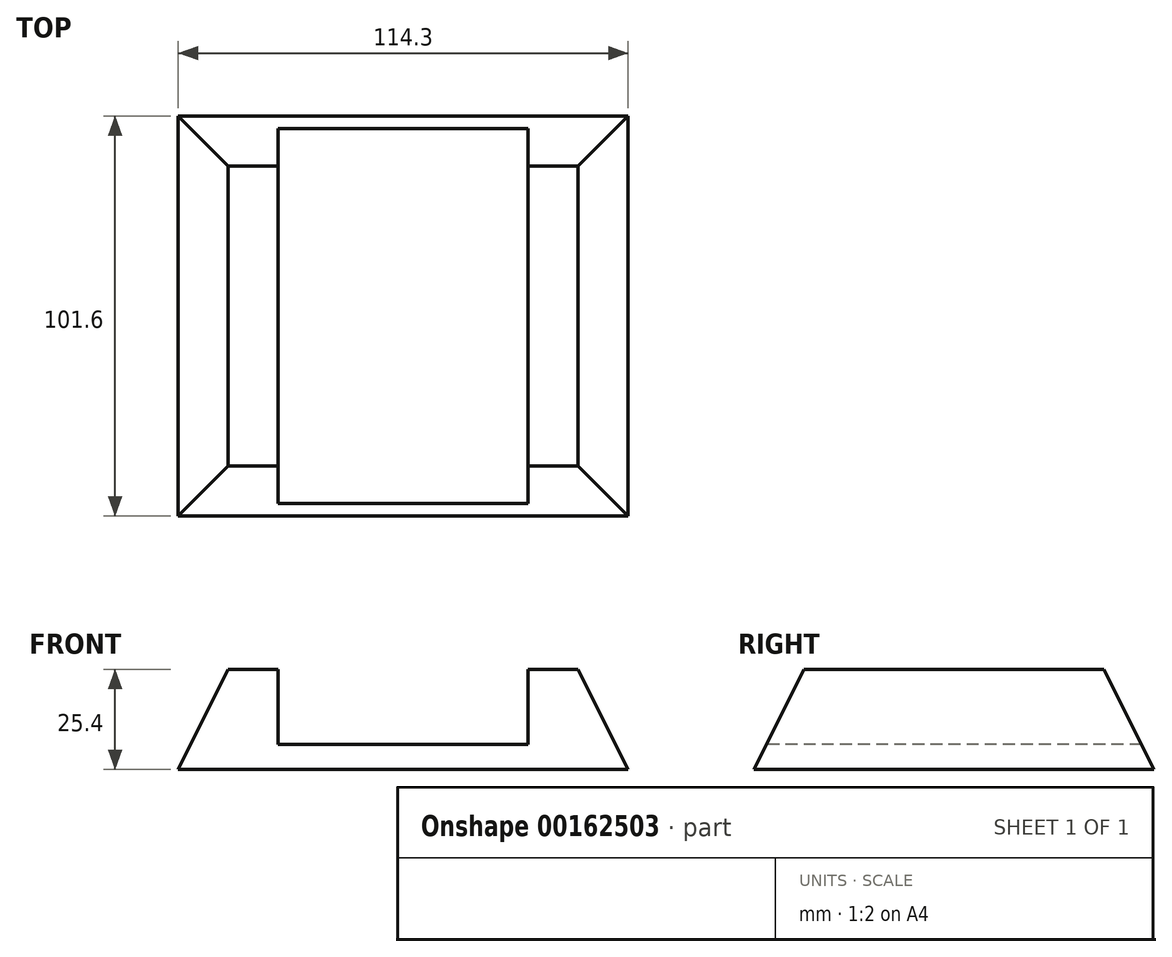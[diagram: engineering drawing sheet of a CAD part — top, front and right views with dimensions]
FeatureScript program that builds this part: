
annotation { "Feature Type Name" : "Feature", "Feature Type Description" : "" }
export const myFeature = defineFeature(function(context is Context, id is Id, definition is map)
    precondition{}
    {
        {
            var Q0;
            Q0=qCreatedBy(makeId("Top.planeOp"),FACE);
            var sketch = newSketch(context, id + "F0", { "sketchPlane" : qUnion([Q0])});
            skLineSegment(sketch, "E0.bottom", {"start": v(-57.15, -50.8) * mm, "end": v(57.15, -50.8) * mm});
            skLineSegment(sketch, "E0.top", {"start": v(-57.15, 50.8) * mm, "end": v(57.15, 50.8) * mm});
            skLineSegment(sketch, "E0.left", {"start": v(-57.15, -50.8) * mm, "end": v(-57.15, 50.8) * mm});
            skLineSegment(sketch, "E0.right", {"start": v(57.15, -50.8) * mm, "end": v(57.15, 50.8) * mm});
            skPoint(sketch, "E0.middle", {"position": v(0, 0) * mm});
            skSolve(sketch);
        }
        {
            var Q0;
            Q0=qCreatedBy(makeId("Top.planeOp"),FACE);
            cPlane(context, id + "F1", {"entities" : qUnion([Q0]), "cplaneType" : CPlaneType.OFFSET, "offset" : 25.4 * mm, "width" : 152.4 * mm, "height" : 152.4 * mm});
        }
        {
            var Q0;
            Q0=qCreatedBy(id+"F1.planeOp",FACE);
            var sketch = newSketch(context, id + "F2", { "sketchPlane" : qUnion([Q0])});
            skLineSegment(sketch, "E1.bottom", {"start": v(-44.45, 38.1) * mm, "end": v(44.45, 38.1) * mm});
            skLineSegment(sketch, "E1.top", {"start": v(-44.45, -38.1) * mm, "end": v(44.45, -38.1) * mm});
            skLineSegment(sketch, "E1.left", {"start": v(-44.45, 38.1) * mm, "end": v(-44.45, -38.1) * mm});
            skLineSegment(sketch, "E1.right", {"start": v(44.45, 38.1) * mm, "end": v(44.45, -38.1) * mm});
            skPoint(sketch, "E1.middle", {"position": v(0, 0) * mm});
            skSolve(sketch);
        }
        {
            var Q0;
            Q0=makeQuery(id+"F2.imprint","IMPRINT",FACE,{"disambiguationData":[TD([[makeQuery(id+"F2.imprint","IMPRINT",EDGE,{"derivedFrom":sQuery(id+"F2.wireOp",EDGE,"E1.bottom")}),-1.0]])]});
            var Q1;
            Q1=makeQuery(id+"F0.imprint","IMPRINT",FACE,{"disambiguationData":[TD([[makeQuery(id+"F0.imprint","IMPRINT",EDGE,{"derivedFrom":sQuery(id+"F0.wireOp",EDGE,"E0.bottom")}),1.0]])]});
            loft(context, id + "F3", {"sheetProfilesArray" : [{ "sheetProfileEntities" : qUnion([Q0]) }, { "sheetProfileEntities" : qUnion([Q1]) }]});
        }
        {
            var Q0;
            Q0=makeQuery(id+"F3.opLoft","CAP_FACE",FACE,{"disambiguationData":[OSD([makeQuery(id+"F2.imprint","IMPRINT",FACE,{"disambiguationData":[TD([[makeQuery(id+"F2.imprint","IMPRINT",EDGE,{"derivedFrom":sQuery(id+"F2.wireOp",EDGE,"E1.bottom")}),-1.0]])]})])],"isStart":true});
            var sketch = newSketch(context, id + "F4", { "sketchPlane" : qUnion([Q0])});
            skLineSegment(sketch, "E2.bottom", {"start": v(-31.75, 96.14) * mm, "end": v(31.75, 96.14) * mm});
            skLineSegment(sketch, "E2.top", {"start": v(-31.75, -96.14) * mm, "end": v(31.75, -96.14) * mm});
            skLineSegment(sketch, "E2.left", {"start": v(-31.75, 96.14) * mm, "end": v(-31.75, -96.14) * mm});
            skLineSegment(sketch, "E2.right", {"start": v(31.75, 96.14) * mm, "end": v(31.75, -96.14) * mm});
            skPoint(sketch, "E2.middle", {"position": v(0, 0) * mm});
            skSolve(sketch);
        }
        {
            var Q0;
            Q0 = qSketchRegion(id + "F4", true);
            extrude(context, id + "F5", {"entities" : qUnion([Q0]), "operationType" : NewBodyOperationType.REMOVE, "oppositeDirection" : true, "depth" : 19.05 * mm, "offsetDistance" : 25.4 * mm});
        }
    });
